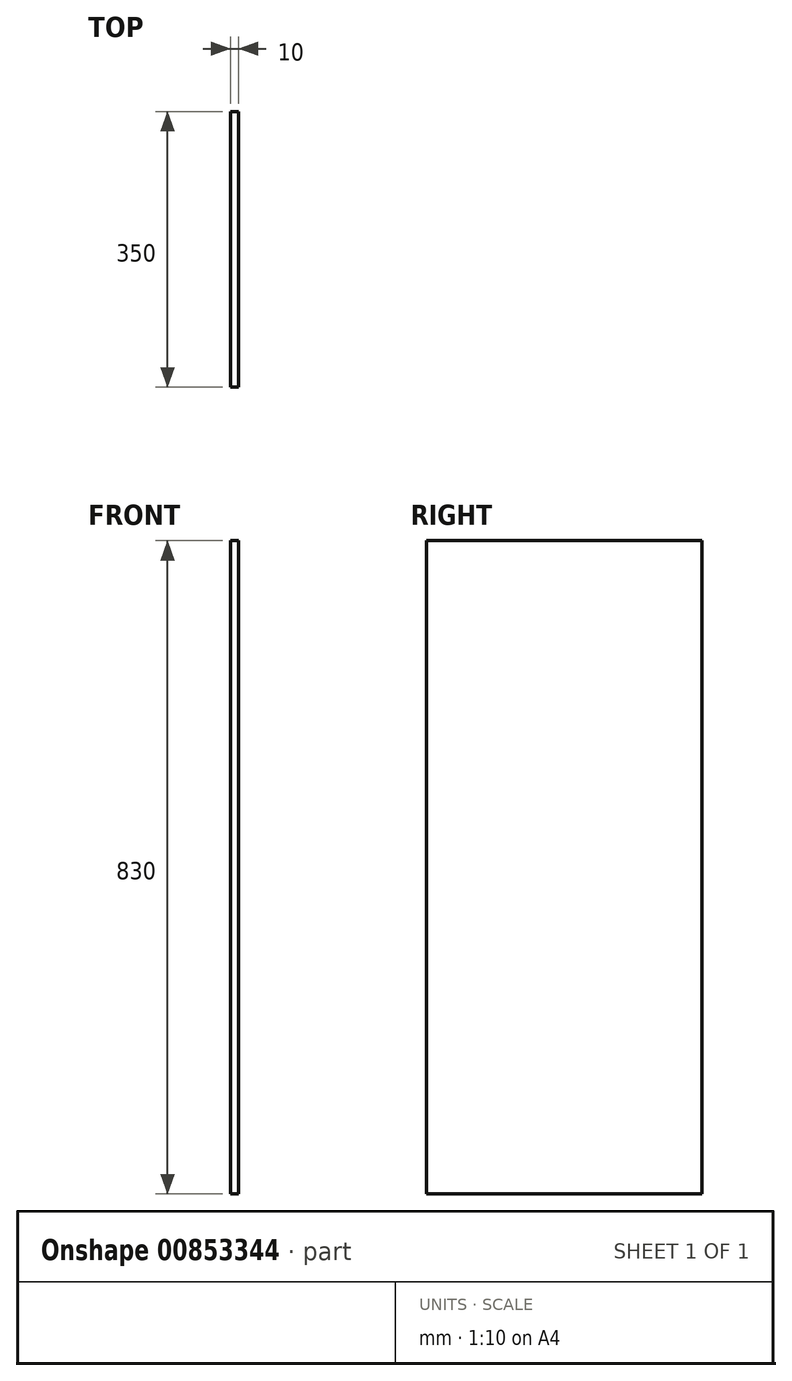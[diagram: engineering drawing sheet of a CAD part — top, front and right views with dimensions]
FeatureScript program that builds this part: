
annotation { "Feature Type Name" : "Feature", "Feature Type Description" : "" }
export const myFeature = defineFeature(function(context is Context, id is Id, definition is map)
    precondition{}
    {
        {
            var Q0;
            Q0=qCreatedBy(makeId("Top.planeOp"),FACE);
            var sketch = newSketch(context, id + "F0", { "sketchPlane" : qUnion([Q0])});
            skLineSegment(sketch, "E0", {"start": v(-6.13, 338.24) * mm, "end": v(3.87, 338.24) * mm});
            skLineSegment(sketch, "E1", {"start": v(-6.13, 338.24) * mm, "end": v(-6.13, -11.76) * mm});
            skLineSegment(sketch, "E2", {"start": v(-6.13, -11.76) * mm, "end": v(3.87, -11.76) * mm});
            skLineSegment(sketch, "E3", {"start": v(3.87, 338.24) * mm, "end": v(3.87, -11.76) * mm});
            skSolve(sketch);
        }
        {
            var Q0;
            Q0 = qSketchRegion(id + "F0", true);
            extrude(context, id + "F1", {"entities" : qUnion([Q0]), "depth" : 830 * mm, "offsetDistance" : 25 * mm});
        }
    });
